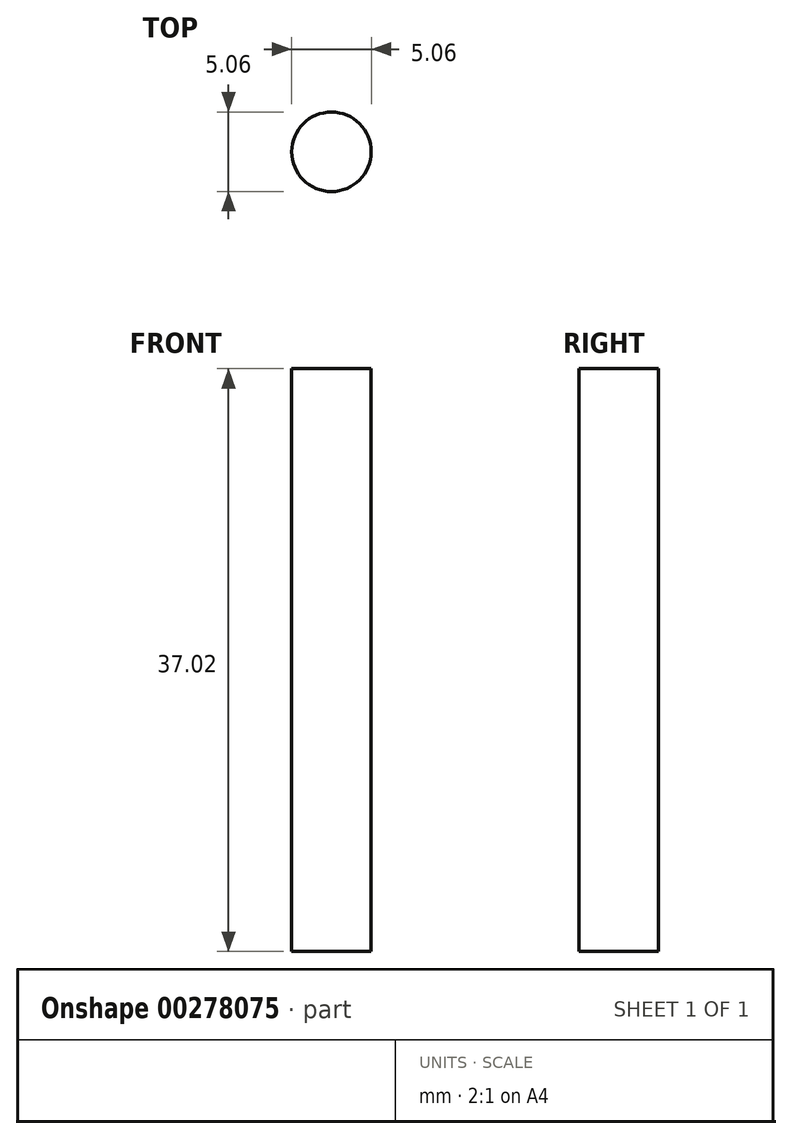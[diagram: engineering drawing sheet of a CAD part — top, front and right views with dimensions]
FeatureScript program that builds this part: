
annotation { "Feature Type Name" : "Feature", "Feature Type Description" : "" }
export const myFeature = defineFeature(function(context is Context, id is Id, definition is map)
    precondition{}
    {
        {
            var Q0;
            Q0=qCreatedBy(makeId("Top.planeOp"),FACE);
            var sketch = newSketch(context, id + "F0", { "sketchPlane" : qUnion([Q0])});
            skCircle(sketch, "E0", {"center": v(0, 0) * mm, "radius": 2.52 * mm});
            skSolve(sketch);
        }
        {
            var Q0;
            Q0 = qSketchRegion(id + "F0", true);
            extrude(context, id + "F1", {"entities" : qUnion([Q0]), "depth" : (16.51 * 2 + 2 + 2) * mm});
        }
    });
